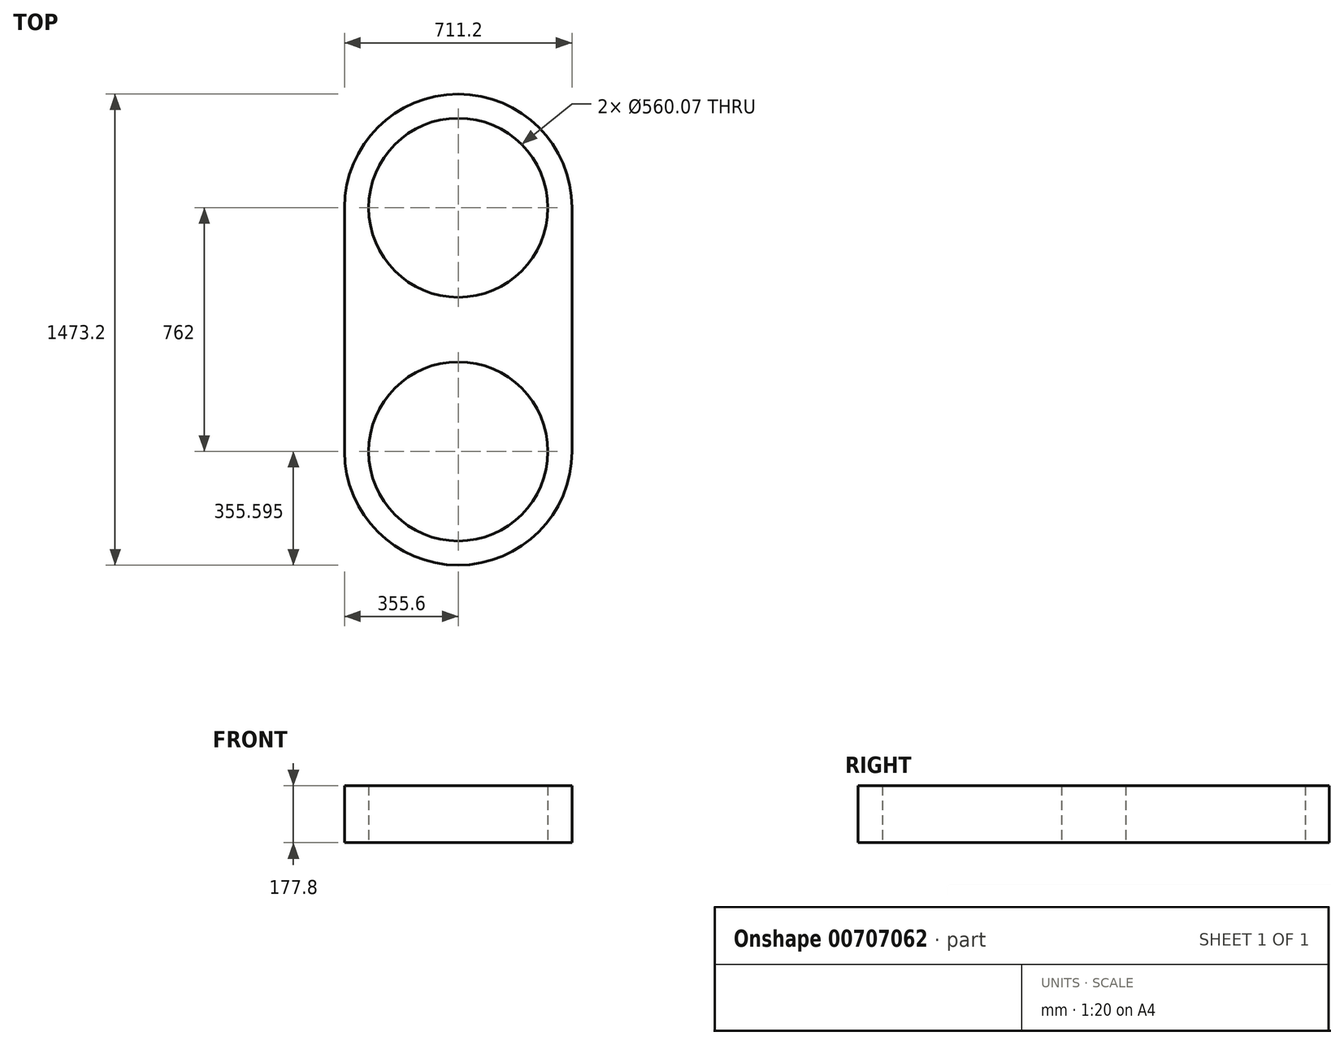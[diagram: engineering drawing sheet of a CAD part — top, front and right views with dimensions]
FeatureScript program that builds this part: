
annotation { "Feature Type Name" : "Feature", "Feature Type Description" : "" }
export const myFeature = defineFeature(function(context is Context, id is Id, definition is map)
    precondition{}
    {
        {
            var Q0;
            Q0=qCreatedBy(makeId("Top.planeOp"),FACE);
            var sketch = newSketch(context, id + "F0", { "sketchPlane" : qUnion([Q0])});
            skLineSegment(sketch, "E0.bottom", {"start": v(0, 248.49) * mm, "end": v(711.2, 248.49) * mm});
            skLineSegment(sketch, "E0.top", {"start": v(0, -513.51) * mm, "end": v(711.2, -513.51) * mm});
            skLineSegment(sketch, "E0.left", {"start": v(0, 248.49) * mm, "end": v(0, -513.51) * mm});
            skLineSegment(sketch, "E0.right", {"start": v(711.2, 248.49) * mm, "end": v(711.2, -513.51) * mm});
            skCircle(sketch, "E1", {"center": v(355.6, -513.51) * mm, "radius": 355.6 * mm});
            skCircle(sketch, "E2", {"center": v(355.6, -513.51) * mm, "radius": 280.04 * mm});
            skCircle(sketch, "E3", {"center": v(355.6, 248.49) * mm, "radius": 355.6 * mm});
            skCircle(sketch, "E4", {"center": v(355.6, 248.49) * mm, "radius": 280.04 * mm});
            skSolve(sketch);
        }
        {
            var Q0;
            {var subQ1=sQuery(id+"F0.wireOp",EDGE,"E0.top");var subQ3=sQuery(id+"F0.wireOp",EDGE,"E2");var subQ4=makeQuery(id+"F0.imprint","INTERSECT",VERTEX,{"disambiguationData":[OD(0.0)],"derivedFrom":[subQ1,subQ3]});Q0=makeQuery(id+"F0.imprint","IMPRINT",FACE,{"disambiguationData":[TD([[makeQuery(id+"F0.imprint","IMPRINT",EDGE,{"disambiguationData":[TD([[subQ4,-1.0]])],"derivedFrom":subQ3}),-1.0]])]});}
            var Q1;
            {var subQ1=sQuery(id+"F0.wireOp",EDGE,"E0.top");var subQ3=sQuery(id+"F0.wireOp",EDGE,"E2");var subQ4=makeQuery(id+"F0.imprint","INTERSECT",VERTEX,{"disambiguationData":[OD(0.0)],"derivedFrom":[subQ1,subQ3]});Q1=makeQuery(id+"F0.imprint","IMPRINT",FACE,{"disambiguationData":[TD([[makeQuery(id+"F0.imprint","IMPRINT",EDGE,{"disambiguationData":[TD([[subQ4,1.0]])],"derivedFrom":subQ3}),-1.0]])]});}
            var Q2;
            {var subQ0=sQuery(id+"F0.wireOp",EDGE,"E0.left");Q2=makeQuery(id+"F0.imprint","IMPRINT",FACE,{"disambiguationData":[TD([[makeQuery(id+"F0.imprint","IMPRINT",EDGE,{"derivedFrom":subQ0}),1.0]])]});}
            var Q3;
            {var subQ1=sQuery(id+"F0.wireOp",EDGE,"E0.bottom");var subQ3=sQuery(id+"F0.wireOp",EDGE,"E4");var subQ4=makeQuery(id+"F0.imprint","INTERSECT",VERTEX,{"disambiguationData":[OD(0.0)],"derivedFrom":[subQ1,subQ3]});Q3=makeQuery(id+"F0.imprint","IMPRINT",FACE,{"disambiguationData":[TD([[makeQuery(id+"F0.imprint","IMPRINT",EDGE,{"disambiguationData":[TD([[subQ4,-1.0]])],"derivedFrom":subQ3}),-1.0]])]});}
            var Q4;
            {var subQ1=sQuery(id+"F0.wireOp",EDGE,"E0.bottom");var subQ3=sQuery(id+"F0.wireOp",EDGE,"E4");var subQ4=makeQuery(id+"F0.imprint","INTERSECT",VERTEX,{"disambiguationData":[OD(0.0)],"derivedFrom":[subQ1,subQ3]});Q4=makeQuery(id+"F0.imprint","IMPRINT",FACE,{"disambiguationData":[TD([[makeQuery(id+"F0.imprint","IMPRINT",EDGE,{"disambiguationData":[TD([[subQ4,1.0]])],"derivedFrom":subQ3}),-1.0]])]});}
            extrude(context, id + "F1", {"entities" : qUnion([Q0, Q1, Q2, Q3, Q4]), "depth" : 177.8 * mm, "offsetDistance" : 25.4 * mm});
        }
    });
